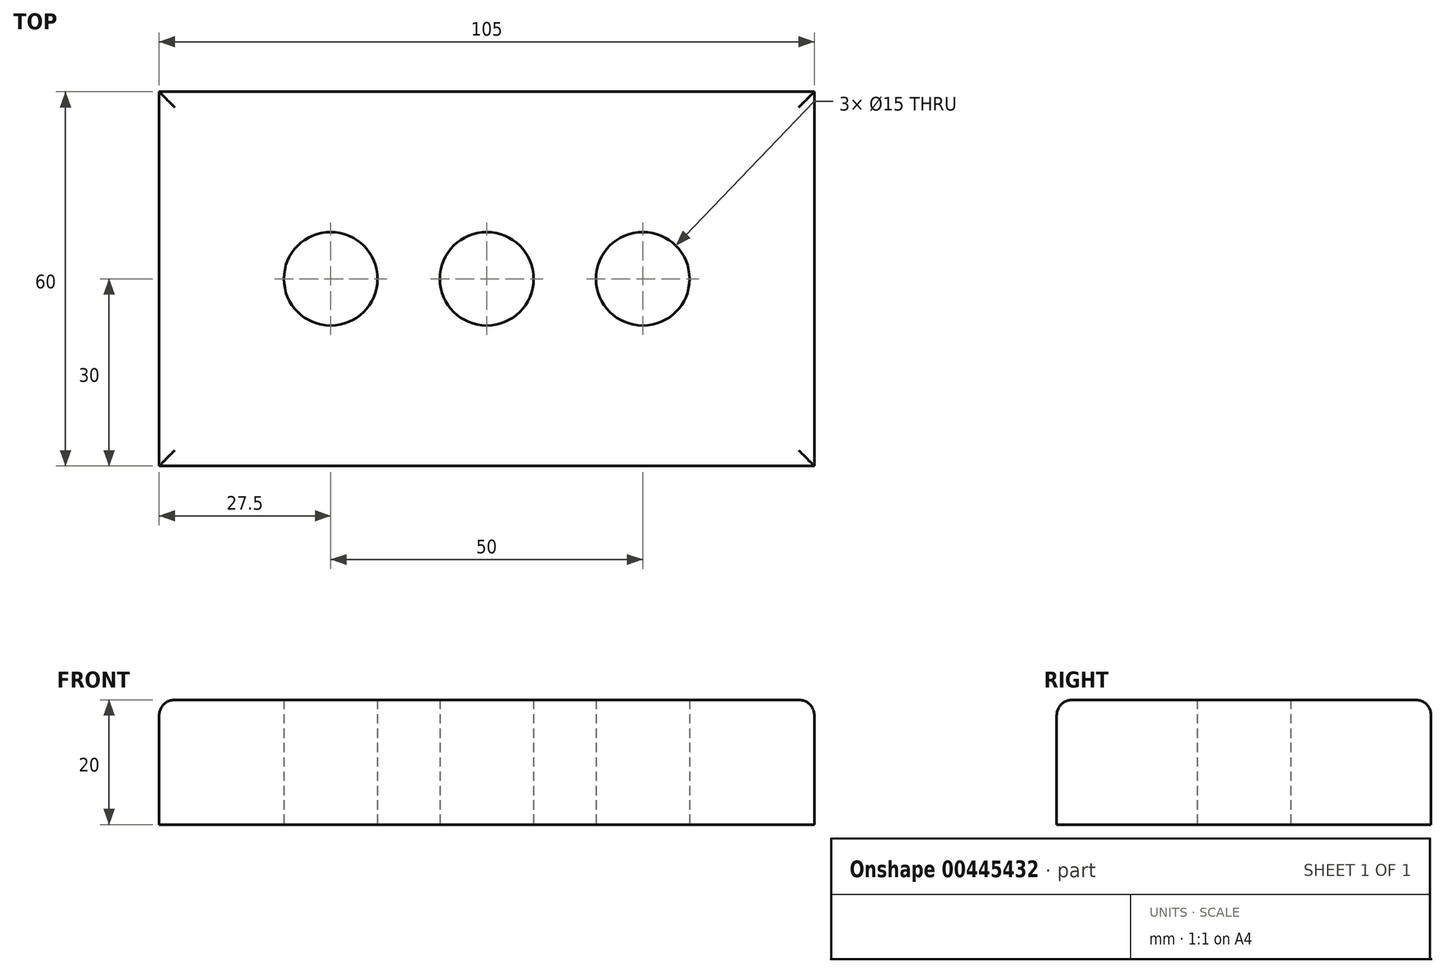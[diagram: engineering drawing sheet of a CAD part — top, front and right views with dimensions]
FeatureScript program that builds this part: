
annotation { "Feature Type Name" : "Feature", "Feature Type Description" : "" }
export const myFeature = defineFeature(function(context is Context, id is Id, definition is map)
    precondition{}
    {
        {
            var Q0;
            Q0=qCreatedBy(makeId("Top.planeOp"),FACE);
            var sketch = newSketch(context, id + "F0", { "sketchPlane" : qUnion([Q0])});
            skLineSegment(sketch, "E0.bottom", {"start": v(-52.5, 30) * mm, "end": v(52.5, 30) * mm});
            skLineSegment(sketch, "E0.top", {"start": v(-52.5, -30) * mm, "end": v(52.5, -30) * mm});
            skLineSegment(sketch, "E0.left", {"start": v(-52.5, 30) * mm, "end": v(-52.5, -30) * mm});
            skLineSegment(sketch, "E0.right", {"start": v(52.5, 30) * mm, "end": v(52.5, -30) * mm});
            skPoint(sketch, "E0.middle", {"position": v(0, 0) * mm});
            skCircle(sketch, "E1", {"center": v(0, 0) * mm, "radius": 7.5 * mm});
            skLineSegment(sketch, "E2", {"start": v(0, 0) * mm, "end": v(-25, 0) * mm});
            skCircle(sketch, "E3", {"center": v(-25, 0) * mm, "radius": 7.5 * mm});
            skLineSegment(sketch, "E4", {"start": v(0, 0) * mm, "end": v(25, 0) * mm});
            skCircle(sketch, "E5", {"center": v(25, 0) * mm, "radius": 7.5 * mm});
            skSolve(sketch);
        }
        {
            var Q0;
            Q0=makeQuery(id+"F0.imprint","IMPRINT",FACE,{"disambiguationData":[TD([[makeQuery(id+"F0.imprint","IMPRINT",EDGE,{"derivedFrom":sQuery(id+"F0.wireOp",EDGE,"E0.bottom")}),-1.0]])]});
            extrude(context, id + "F1", {"entities" : qUnion([Q0]), "depth" : 20 * mm});
        }
        {
            var Q0;
            Q0=makeQuery(id+"F1.opExtrude","CAP_EDGE",EDGE,{"disambiguationData":[OSD([sQuery(id+"F0.wireOp",EDGE,"E0.left")])],"isStart":false});
            var Q1;
            Q1=makeQuery(id+"F1.opExtrude","CAP_EDGE",EDGE,{"disambiguationData":[OSD([sQuery(id+"F0.wireOp",EDGE,"E0.bottom")])],"isStart":false});
            var Q2;
            Q2=makeQuery(id+"F1.opExtrude","CAP_EDGE",EDGE,{"disambiguationData":[OSD([sQuery(id+"F0.wireOp",EDGE,"E0.right")])],"isStart":false});
            var Q3;
            Q3=makeQuery(id+"F1.opExtrude","CAP_EDGE",EDGE,{"disambiguationData":[OSD([sQuery(id+"F0.wireOp",EDGE,"E0.top")])],"isStart":false});
            fillet(context, id + "F2", {"entities" : qUnion([Q0, Q1, Q2, Q3]), "radius" : 2.5 * mm, "tangentPropagation" : true, "allowEdgeOverflow" : false});
        }
    });
